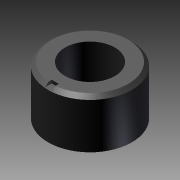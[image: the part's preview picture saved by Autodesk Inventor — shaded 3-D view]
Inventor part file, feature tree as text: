
AUTODESK INVENTOR PART (.ipt)
format: ipt  version: 2011 SP1 (Build 150282100, 282)  size: 105,984 bytes
history: native  units: in
note: dims shown in document units (in); Inventor stores cm internally (conversion verified against a paired STEP export)
features: other x14, sketch x2, revolve x1, extrude x1
ambient origin geometry x8: Origin, YZ Plane, XZ Plane, XY Plane, X Axis, Y Axis, Z Axis, Center Point
bodies: Solid1 (feature_tree), body_straight_XY (feature_tree), body_straight_YZ (feature_tree), body_straight_ZX (feature_tree), body_straight_X (feature_tree), body_straight_Y (feature_tree), body_straight_Z (feature_tree), body_straight_Center (feature_tree), body_ver_ra_XY (feature_tree), body_ver_ra_YZ (feature_tree), body_ver_ra_ZX (feature_tree), body_ver_ra_X (feature_tree), body_ver_ra_Y (feature_tree), body_ver_ra_Z (feature_tree), body_ver_ra_Center (feature_tree)
feature tree (18):
  revolve  "Revolution1"  [1 undecoded]
  extrude  "Extrusion1"  [1 undecoded]
  other  "cp_toggle__straight_XY"
  other  "cp_toggle__straight_YZ"
  other  "cp_toggle__straight_ZX"
  other  "cp_toggle__straight_X"
  other  "cp_toggle__straight_Y"
  other  "cp_toggle__straight_Z"
  other  "cp_toggle__straight_Center"
  other  "toggle_vrtira_XY"
  other  "toggle_vrtira_YZ"
  other  "toggle_vrtira_ZX"
  other  "toggle_vrtira_X"
  other  "toggle_vrtira_Y"
  other  "toggle_vrtira_Z"
  other  "toggle_vrtira_Center"
  sketch  "Sketch_1"  dims[d0=360.0deg d1=0.009in d2=0.0in]
  sketch  "Sketch_10"
note: 2 required parameter values undecoded (feature->parameter linkage not recoverable at this tier; creation-order binding heuristic only, values carry confidence <= 0.55)